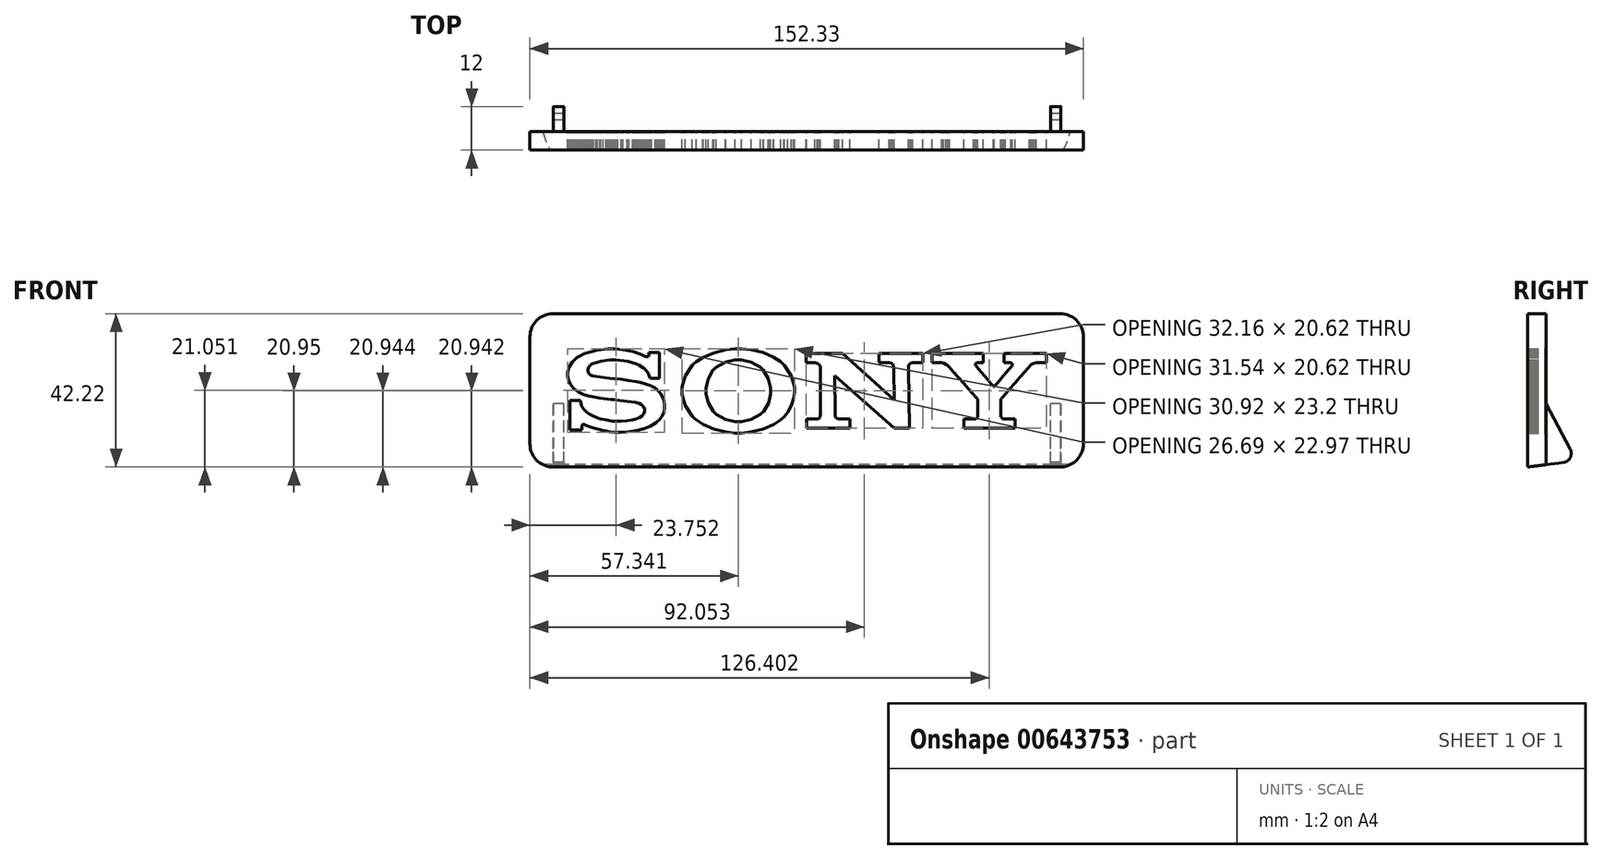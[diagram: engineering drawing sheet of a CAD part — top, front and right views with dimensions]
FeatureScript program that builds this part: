
annotation { "Feature Type Name" : "Feature", "Feature Type Description" : "" }
export const myFeature = defineFeature(function(context is Context, id is Id, definition is map)
    precondition{}
    {
        {
            var Q0;
            Q0=qCreatedBy(makeId("Right.planeOp"),FACE);
            cPlane(context, id + "F0", {"entities" : qUnion([Q0]), "cplaneType" : CPlaneType.OFFSET, "offset" : 69.85 * mm, "width" : 152.4 * mm, "height" : 152.4 * mm});
        }
        {
            var Q0;
            Q0=qCreatedBy(makeId("Right.planeOp"),FACE);
            cPlane(context, id + "F1", {"entities" : qUnion([Q0]), "cplaneType" : CPlaneType.OFFSET, "offset" : 69.85 * mm, "oppositeDirection" : true, "width" : 152.4 * mm, "height" : 152.4 * mm});
        }
        {
            var Q0;
            Q0=qCreatedBy(makeId("Front.planeOp"),FACE);
            var sketch = newSketch(context, id + "F2", { "sketchPlane" : qUnion([Q0])});
            skLineSegment(sketch, "E0.bottom", {"start": v(-69.94, 21.27) * mm, "end": v(69.7, 21.27) * mm});
            skLineSegment(sketch, "E0.top", {"start": v(-69.94, -20.96) * mm, "end": v(69.7, -20.96) * mm});
            skLineSegment(sketch, "E0.left", {"start": v(-76.3, 14.92) * mm, "end": v(-76.3, -14.61) * mm});
            skLineSegment(sketch, "E0.right", {"start": v(76.04, 14.92) * mm, "end": v(76.04, -14.61) * mm});
            skPoint(sketch, "E1.visualSharp", {"position": v(-76.3, 21.27) * mm});
            skArc(sketch, "E1.filletArc", {"start": v(-69.94, 21.27) * mm, "mid": v(-74.43, 19.41) * mm, "end": v(-76.3, 14.92) * mm});
            skPoint(sketch, "E2.visualSharp", {"position": v(-76.3, -20.96) * mm});
            skArc(sketch, "E2.filletArc", {"start": v(-76.3, -14.61) * mm, "mid": v(-74.43, -19.1) * mm, "end": v(-69.94, -20.96) * mm});
            skPoint(sketch, "E3.visualSharp", {"position": v(76.04, 21.27) * mm});
            skArc(sketch, "E3.filletArc", {"start": v(76.04, 14.92) * mm, "mid": v(74.18, 19.41) * mm, "end": v(69.7, 21.27) * mm});
            skPoint(sketch, "E4.visualSharp", {"position": v(76.04, -20.96) * mm});
            skArc(sketch, "E4.filletArc", {"start": v(69.7, -20.96) * mm, "mid": v(74.18, -19.1) * mm, "end": v(76.04, -14.61) * mm});
            skSolve(sketch);
        }
        {
            var Q0;
            Q0 = qSketchRegion(id + "F2", true);
            extrude(context, id + "F3", {"entities" : qUnion([Q0]), "endBound" : BoundingType.SYMMETRIC, "depth" : 5.08 * mm, "offsetDistance" : 25.4 * mm});
        }
        {
            var Q0;
            Q0=qCreatedBy(makeId("Front.planeOp"),FACE);
            var sketch = newSketch(context, id + "F4", { "sketchPlane" : qUnion([Q0])});
            skLineSegment(sketch, "E5", {"start": v(-18.94, -11.6) * mm, "end": v(-19.81, -11.6) * mm});
            skLineSegment(sketch, "E6", {"start": v(-19.81, -11.6) * mm, "end": v(-22.44, -11.33) * mm});
            skLineSegment(sketch, "E7", {"start": v(-22.44, -11.33) * mm, "end": v(-25.7, -10.55) * mm});
            skLineSegment(sketch, "E8", {"start": v(-25.7, -10.55) * mm, "end": v(-28.62, -9.27) * mm});
            skLineSegment(sketch, "E9", {"start": v(-28.62, -9.27) * mm, "end": v(-30.54, -8.02) * mm});
            skLineSegment(sketch, "E10", {"start": v(-30.54, -8.02) * mm, "end": v(-31.1, -7.51) * mm});
            skLineSegment(sketch, "E11", {"start": v(-31.1, -7.51) * mm, "end": v(-31.66, -7.01) * mm});
            skLineSegment(sketch, "E12", {"start": v(-31.66, -7.01) * mm, "end": v(-33.6, -4.05) * mm});
            skLineSegment(sketch, "E13", {"start": v(-33.6, -4.05) * mm, "end": v(-34.4, -1) * mm});
            skLineSegment(sketch, "E14", {"start": v(-34.4, -1) * mm, "end": v(-34.4, 0.02) * mm});
            skLineSegment(sketch, "E15", {"start": v(-34.4, 0.02) * mm, "end": v(-34.4, 1.03) * mm});
            skLineSegment(sketch, "E16", {"start": v(-34.4, 1.03) * mm, "end": v(-33.58, 4.07) * mm});
            skLineSegment(sketch, "E17", {"start": v(-33.58, 4.07) * mm, "end": v(-31.65, 7.03) * mm});
            skLineSegment(sketch, "E18", {"start": v(-31.65, 7.03) * mm, "end": v(-31.1, 7.53) * mm});
            skLineSegment(sketch, "E19", {"start": v(-31.1, 7.53) * mm, "end": v(-30.56, 8.02) * mm});
            skLineSegment(sketch, "E20", {"start": v(-30.56, 8.02) * mm, "end": v(-28.69, 9.22) * mm});
            skLineSegment(sketch, "E21", {"start": v(-28.69, 9.22) * mm, "end": v(-25.7, 10.5) * mm});
            skLineSegment(sketch, "E22", {"start": v(-25.7, 10.5) * mm, "end": v(-22.38, 11.32) * mm});
            skLineSegment(sketch, "E23", {"start": v(-22.38, 11.32) * mm, "end": v(-19.8, 11.6) * mm});
            skLineSegment(sketch, "E24", {"start": v(-19.8, 11.6) * mm, "end": v(-18.94, 11.6) * mm});
            skLineSegment(sketch, "E25", {"start": v(-18.94, 11.6) * mm, "end": v(-18.04, 11.6) * mm});
            skLineSegment(sketch, "E26", {"start": v(-18.04, 11.6) * mm, "end": v(-15.34, 11.36) * mm});
            skLineSegment(sketch, "E27", {"start": v(-15.34, 11.36) * mm, "end": v(-12.11, 10.61) * mm});
            skLineSegment(sketch, "E28", {"start": v(-12.11, 10.61) * mm, "end": v(-9.25, 9.34) * mm});
            skLineSegment(sketch, "E29", {"start": v(-9.25, 9.34) * mm, "end": v(-7.32, 8.04) * mm});
            skLineSegment(sketch, "E30", {"start": v(-7.32, 8.04) * mm, "end": v(-6.75, 7.52) * mm});
            skLineSegment(sketch, "E31", {"start": v(-6.75, 7.52) * mm, "end": v(-6.2, 7.02) * mm});
            skLineSegment(sketch, "E32", {"start": v(-6.2, 7.02) * mm, "end": v(-4.3, 4.06) * mm});
            skLineSegment(sketch, "E33", {"start": v(-4.3, 4.06) * mm, "end": v(-3.49, 1.03) * mm});
            skLineSegment(sketch, "E34", {"start": v(-3.49, 1.03) * mm, "end": v(-3.49, 0.02) * mm});
            skLineSegment(sketch, "E35", {"start": v(-3.49, 0.02) * mm, "end": v(-3.49, -0.49) * mm});
            skLineSegment(sketch, "E36", {"start": v(-3.49, -0.49) * mm, "end": v(-3.7, -2.01) * mm});
            skLineSegment(sketch, "E37", {"start": v(-3.7, -2.01) * mm, "end": v(-4.32, -4.01) * mm});
            skLineSegment(sketch, "E38", {"start": v(-4.32, -4.01) * mm, "end": v(-5.34, -5.88) * mm});
            skLineSegment(sketch, "E39", {"start": v(-5.34, -5.88) * mm, "end": v(-6.36, -7.15) * mm});
            skLineSegment(sketch, "E40", {"start": v(-6.36, -7.15) * mm, "end": v(-6.75, -7.51) * mm});
            skLineSegment(sketch, "E41", {"start": v(-6.75, -7.51) * mm, "end": v(-7.3, -8.02) * mm});
            skLineSegment(sketch, "E42", {"start": v(-7.3, -8.02) * mm, "end": v(-9.2, -9.28) * mm});
            skLineSegment(sketch, "E43", {"start": v(-9.2, -9.28) * mm, "end": v(-12.13, -10.56) * mm});
            skLineSegment(sketch, "E44", {"start": v(-12.13, -10.56) * mm, "end": v(-15.42, -11.34) * mm});
            skLineSegment(sketch, "E45", {"start": v(-15.42, -11.34) * mm, "end": v(-18.06, -11.6) * mm});
            skLineSegment(sketch, "E46", {"start": v(-18.06, -11.6) * mm, "end": v(-18.94, -11.6) * mm});
            skLineSegment(sketch, "E47", {"start": v(-18.94, -11.6) * mm, "end": v(-18.94, -8.54) * mm});
            skLineSegment(sketch, "E48", {"start": v(-18.94, -8.54) * mm, "end": v(-18.04, -8.54) * mm});
            skLineSegment(sketch, "E49", {"start": v(-18.04, -8.54) * mm, "end": v(-15.34, -7.9) * mm});
            skLineSegment(sketch, "E50", {"start": v(-15.34, -7.9) * mm, "end": v(-12.83, -6.44) * mm});
            skLineSegment(sketch, "E51", {"start": v(-12.83, -6.44) * mm, "end": v(-12.41, -6.03) * mm});
            skLineSegment(sketch, "E52", {"start": v(-12.41, -6.03) * mm, "end": v(-12, -5.63) * mm});
            skLineSegment(sketch, "E53", {"start": v(-12, -5.63) * mm, "end": v(-10.61, -3.31) * mm});
            skLineSegment(sketch, "E54", {"start": v(-10.61, -3.31) * mm, "end": v(-10.03, -0.81) * mm});
            skLineSegment(sketch, "E55", {"start": v(-10.03, -0.81) * mm, "end": v(-10.03, 0.02) * mm});
            skLineSegment(sketch, "E56", {"start": v(-10.03, 0.02) * mm, "end": v(-10.03, 0.85) * mm});
            skLineSegment(sketch, "E57", {"start": v(-10.03, 0.85) * mm, "end": v(-10.63, 3.35) * mm});
            skLineSegment(sketch, "E58", {"start": v(-10.63, 3.35) * mm, "end": v(-12.02, 5.7) * mm});
            skLineSegment(sketch, "E59", {"start": v(-12.02, 5.7) * mm, "end": v(-12.41, 6.09) * mm});
            skLineSegment(sketch, "E60", {"start": v(-12.41, 6.09) * mm, "end": v(-12.82, 6.49) * mm});
            skLineSegment(sketch, "E61", {"start": v(-12.82, 6.49) * mm, "end": v(-15.35, 7.93) * mm});
            skLineSegment(sketch, "E62", {"start": v(-15.35, 7.93) * mm, "end": v(-18.04, 8.58) * mm});
            skLineSegment(sketch, "E63", {"start": v(-18.04, 8.58) * mm, "end": v(-18.94, 8.58) * mm});
            skLineSegment(sketch, "E64", {"start": v(-18.94, 8.58) * mm, "end": v(-19.84, 8.58) * mm});
            skLineSegment(sketch, "E65", {"start": v(-19.84, 8.58) * mm, "end": v(-22.54, 7.93) * mm});
            skLineSegment(sketch, "E66", {"start": v(-22.54, 7.93) * mm, "end": v(-25.07, 6.49) * mm});
            skLineSegment(sketch, "E67", {"start": v(-25.07, 6.49) * mm, "end": v(-25.48, 6.09) * mm});
            skLineSegment(sketch, "E68", {"start": v(-25.48, 6.09) * mm, "end": v(-25.87, 5.7) * mm});
            skLineSegment(sketch, "E69", {"start": v(-25.87, 5.7) * mm, "end": v(-27.25, 3.35) * mm});
            skLineSegment(sketch, "E70", {"start": v(-27.25, 3.35) * mm, "end": v(-27.86, 0.85) * mm});
            skLineSegment(sketch, "E71", {"start": v(-27.86, 0.85) * mm, "end": v(-27.86, 0.02) * mm});
            skLineSegment(sketch, "E72", {"start": v(-27.86, 0.02) * mm, "end": v(-27.86, -0.8) * mm});
            skLineSegment(sketch, "E73", {"start": v(-27.86, -0.8) * mm, "end": v(-27.25, -3.3) * mm});
            skLineSegment(sketch, "E74", {"start": v(-27.25, -3.3) * mm, "end": v(-25.86, -5.65) * mm});
            skLineSegment(sketch, "E75", {"start": v(-25.86, -5.65) * mm, "end": v(-25.48, -6.03) * mm});
            skLineSegment(sketch, "E76", {"start": v(-25.48, -6.03) * mm, "end": v(-25.07, -6.43) * mm});
            skLineSegment(sketch, "E77", {"start": v(-25.07, -6.43) * mm, "end": v(-22.54, -7.9) * mm});
            skLineSegment(sketch, "E78", {"start": v(-22.54, -7.9) * mm, "end": v(-19.84, -8.54) * mm});
            skLineSegment(sketch, "E79", {"start": v(-19.84, -8.54) * mm, "end": v(-18.94, -8.54) * mm});
            skLineSegment(sketch, "E80", {"start": v(-18.94, -8.54) * mm, "end": v(-18.94, -11.6) * mm});
            skLineSegment(sketch, "E81", {"start": v(-53.83, 11.59) * mm, "end": v(-54.83, 11.59) * mm});
            skLineSegment(sketch, "E82", {"start": v(-54.83, 11.59) * mm, "end": v(-57.82, 11.21) * mm});
            skLineSegment(sketch, "E83", {"start": v(-57.82, 11.21) * mm, "end": v(-61.13, 10.29) * mm});
            skLineSegment(sketch, "E84", {"start": v(-61.13, 10.29) * mm, "end": v(-61.74, 10.01) * mm});
            skLineSegment(sketch, "E85", {"start": v(-61.74, 10.01) * mm, "end": v(-62.16, 9.82) * mm});
            skLineSegment(sketch, "E86", {"start": v(-62.16, 9.82) * mm, "end": v(-63.35, 9.12) * mm});
            skLineSegment(sketch, "E87", {"start": v(-63.35, 9.12) * mm, "end": v(-64.67, 7.96) * mm});
            skLineSegment(sketch, "E88", {"start": v(-64.67, 7.96) * mm, "end": v(-65.56, 6.48) * mm});
            skLineSegment(sketch, "E89", {"start": v(-65.56, 6.48) * mm, "end": v(-65.88, 5.1) * mm});
            skLineSegment(sketch, "E90", {"start": v(-65.88, 5.1) * mm, "end": v(-65.88, 4.63) * mm});
            skLineSegment(sketch, "E91", {"start": v(-65.88, 4.63) * mm, "end": v(-65.88, 4.22) * mm});
            skLineSegment(sketch, "E92", {"start": v(-65.88, 4.22) * mm, "end": v(-65.64, 3) * mm});
            skLineSegment(sketch, "E93", {"start": v(-65.64, 3) * mm, "end": v(-65.1, 1.77) * mm});
            skLineSegment(sketch, "E94", {"start": v(-65.1, 1.77) * mm, "end": v(-64.59, 1.03) * mm});
            skLineSegment(sketch, "E95", {"start": v(-64.59, 1.03) * mm, "end": v(-64.37, 0.79) * mm});
            skLineSegment(sketch, "E96", {"start": v(-64.37, 0.79) * mm, "end": v(-64.22, 0.65) * mm});
            skLineSegment(sketch, "E97", {"start": v(-64.22, 0.65) * mm, "end": v(-63.77, 0.26) * mm});
            skLineSegment(sketch, "E98", {"start": v(-63.77, 0.26) * mm, "end": v(-62.9, -0.34) * mm});
            skLineSegment(sketch, "E99", {"start": v(-62.9, -0.34) * mm, "end": v(-61.64, -0.95) * mm});
            skLineSegment(sketch, "E100", {"start": v(-61.64, -0.95) * mm, "end": v(-60.3, -1.37) * mm});
            skLineSegment(sketch, "E101", {"start": v(-60.3, -1.37) * mm, "end": v(-59.85, -1.47) * mm});
            skLineSegment(sketch, "E102", {"start": v(-59.85, -1.47) * mm, "end": v(-59.54, -1.54) * mm});
            skLineSegment(sketch, "E103", {"start": v(-59.54, -1.54) * mm, "end": v(-57.1, -1.95) * mm});
            skLineSegment(sketch, "E104", {"start": v(-57.1, -1.95) * mm, "end": v(-53.95, -2.37) * mm});
            skLineSegment(sketch, "E105", {"start": v(-53.95, -2.37) * mm, "end": v(-53.29, -2.44) * mm});
            skLineSegment(sketch, "E106", {"start": v(-53.29, -2.44) * mm, "end": v(-52.63, -2.5) * mm});
            skLineSegment(sketch, "E107", {"start": v(-52.63, -2.5) * mm, "end": v(-49.55, -2.85) * mm});
            skLineSegment(sketch, "E108", {"start": v(-49.55, -2.85) * mm, "end": v(-47.27, -3.18) * mm});
            skLineSegment(sketch, "E109", {"start": v(-47.27, -3.18) * mm, "end": v(-47, -3.25) * mm});
            skLineSegment(sketch, "E110", {"start": v(-47, -3.25) * mm, "end": v(-46.83, -3.3) * mm});
            skLineSegment(sketch, "E111", {"start": v(-46.83, -3.3) * mm, "end": v(-46.3, -3.44) * mm});
            skLineSegment(sketch, "E112", {"start": v(-46.3, -3.44) * mm, "end": v(-45.57, -3.78) * mm});
            skLineSegment(sketch, "E113", {"start": v(-45.57, -3.78) * mm, "end": v(-45, -4.37) * mm});
            skLineSegment(sketch, "E114", {"start": v(-45, -4.37) * mm, "end": v(-44.76, -5.1) * mm});
            skLineSegment(sketch, "E115", {"start": v(-44.76, -5.1) * mm, "end": v(-44.76, -5.34) * mm});
            skLineSegment(sketch, "E116", {"start": v(-44.76, -5.34) * mm, "end": v(-44.76, -5.58) * mm});
            skLineSegment(sketch, "E117", {"start": v(-44.76, -5.58) * mm, "end": v(-45, -6.32) * mm});
            skLineSegment(sketch, "E118", {"start": v(-45, -6.32) * mm, "end": v(-45.53, -6.97) * mm});
            skLineSegment(sketch, "E119", {"start": v(-45.53, -6.97) * mm, "end": v(-46.12, -7.33) * mm});
            skLineSegment(sketch, "E120", {"start": v(-46.12, -7.33) * mm, "end": v(-46.44, -7.47) * mm});
            skLineSegment(sketch, "E121", {"start": v(-46.44, -7.47) * mm, "end": v(-46.5, -7.5) * mm});
            skLineSegment(sketch, "E122", {"start": v(-46.5, -7.5) * mm, "end": v(-46.56, -7.52) * mm});
            skLineSegment(sketch, "E123", {"start": v(-46.56, -7.52) * mm, "end": v(-46.98, -7.68) * mm});
            skLineSegment(sketch, "E124", {"start": v(-46.98, -7.68) * mm, "end": v(-48.02, -8) * mm});
            skLineSegment(sketch, "E125", {"start": v(-48.02, -8) * mm, "end": v(-49.6, -8.28) * mm});
            skLineSegment(sketch, "E126", {"start": v(-49.6, -8.28) * mm, "end": v(-51.2, -8.41) * mm});
            skLineSegment(sketch, "E127", {"start": v(-51.2, -8.41) * mm, "end": v(-51.74, -8.41) * mm});
            skLineSegment(sketch, "E128", {"start": v(-51.74, -8.41) * mm, "end": v(-52.2, -8.41) * mm});
            skLineSegment(sketch, "E129", {"start": v(-52.2, -8.41) * mm, "end": v(-53.57, -8.3) * mm});
            skLineSegment(sketch, "E130", {"start": v(-53.57, -8.3) * mm, "end": v(-55.36, -8.01) * mm});
            skLineSegment(sketch, "E131", {"start": v(-55.36, -8.01) * mm, "end": v(-56.9, -7.66) * mm});
            skLineSegment(sketch, "E132", {"start": v(-56.9, -7.66) * mm, "end": v(-57.72, -7.42) * mm});
            skLineSegment(sketch, "E133", {"start": v(-57.72, -7.42) * mm, "end": v(-57.98, -7.33) * mm});
            skLineSegment(sketch, "E134", {"start": v(-57.98, -7.33) * mm, "end": v(-58.2, -7.25) * mm});
            skLineSegment(sketch, "E135", {"start": v(-58.2, -7.25) * mm, "end": v(-58.88, -6.98) * mm});
            skLineSegment(sketch, "E136", {"start": v(-58.88, -6.98) * mm, "end": v(-59.8, -6.5) * mm});
            skLineSegment(sketch, "E137", {"start": v(-59.8, -6.5) * mm, "end": v(-60.7, -5.84) * mm});
            skLineSegment(sketch, "E138", {"start": v(-60.7, -5.84) * mm, "end": v(-61.4, -5.16) * mm});
            skLineSegment(sketch, "E139", {"start": v(-61.4, -5.16) * mm, "end": v(-61.6, -4.92) * mm});
            skLineSegment(sketch, "E140", {"start": v(-61.6, -4.92) * mm, "end": v(-61.66, -4.83) * mm});
            skLineSegment(sketch, "E141", {"start": v(-61.66, -4.83) * mm, "end": v(-61.83, -4.55) * mm});
            skLineSegment(sketch, "E142", {"start": v(-61.83, -4.55) * mm, "end": v(-62.08, -4) * mm});
            skLineSegment(sketch, "E143", {"start": v(-62.08, -4) * mm, "end": v(-62.27, -3.34) * mm});
            skLineSegment(sketch, "E144", {"start": v(-62.27, -3.34) * mm, "end": v(-62.34, -2.8) * mm});
            skLineSegment(sketch, "E145", {"start": v(-62.34, -2.8) * mm, "end": v(-62.34, -2.63) * mm});
            skLineSegment(sketch, "E146", {"start": v(-62.34, -2.63) * mm, "end": v(-65.24, -2.63) * mm});
            skLineSegment(sketch, "E147", {"start": v(-65.24, -2.63) * mm, "end": v(-65.24, -10.75) * mm});
            skLineSegment(sketch, "E148", {"start": v(-65.24, -10.75) * mm, "end": v(-62.02, -10.75) * mm});
            skLineSegment(sketch, "E149", {"start": v(-62.02, -10.75) * mm, "end": v(-62.02, -9.65) * mm});
            skLineSegment(sketch, "E150", {"start": v(-62.02, -9.65) * mm, "end": v(-62.02, -9.61) * mm});
            skLineSegment(sketch, "E151", {"start": v(-62.02, -9.61) * mm, "end": v(-61.99, -9.5) * mm});
            skLineSegment(sketch, "E152", {"start": v(-61.99, -9.5) * mm, "end": v(-61.87, -9.31) * mm});
            skLineSegment(sketch, "E153", {"start": v(-61.87, -9.31) * mm, "end": v(-61.66, -9.2) * mm});
            skLineSegment(sketch, "E154", {"start": v(-61.66, -9.2) * mm, "end": v(-61.4, -9.22) * mm});
            skLineSegment(sketch, "E155", {"start": v(-61.4, -9.22) * mm, "end": v(-61.32, -9.25) * mm});
            skLineSegment(sketch, "E156", {"start": v(-61.32, -9.25) * mm, "end": v(-61.15, -9.33) * mm});
            skLineSegment(sketch, "E157", {"start": v(-61.15, -9.33) * mm, "end": v(-60.6, -9.56) * mm});
            skLineSegment(sketch, "E158", {"start": v(-60.6, -9.56) * mm, "end": v(-59.49, -9.97) * mm});
            skLineSegment(sketch, "E159", {"start": v(-59.49, -9.97) * mm, "end": v(-58.12, -10.4) * mm});
            skLineSegment(sketch, "E160", {"start": v(-58.12, -10.4) * mm, "end": v(-57, -10.7) * mm});
            skLineSegment(sketch, "E161", {"start": v(-57, -10.7) * mm, "end": v(-56.6, -10.78) * mm});
            skLineSegment(sketch, "E162", {"start": v(-56.6, -10.78) * mm, "end": v(-56.31, -10.84) * mm});
            skLineSegment(sketch, "E163", {"start": v(-56.31, -10.84) * mm, "end": v(-55.43, -11.02) * mm});
            skLineSegment(sketch, "E164", {"start": v(-55.43, -11.02) * mm, "end": v(-54.32, -11.21) * mm});
            skLineSegment(sketch, "E165", {"start": v(-54.32, -11.21) * mm, "end": v(-53.14, -11.34) * mm});
            skLineSegment(sketch, "E166", {"start": v(-53.14, -11.34) * mm, "end": v(-52.08, -11.39) * mm});
            skLineSegment(sketch, "E167", {"start": v(-52.08, -11.39) * mm, "end": v(-51.72, -11.39) * mm});
            skLineSegment(sketch, "E168", {"start": v(-51.72, -11.39) * mm, "end": v(-51.15, -11.39) * mm});
            skLineSegment(sketch, "E169", {"start": v(-51.15, -11.39) * mm, "end": v(-49.43, -11.3) * mm});
            skLineSegment(sketch, "E170", {"start": v(-49.43, -11.3) * mm, "end": v(-47.64, -11.06) * mm});
            skLineSegment(sketch, "E171", {"start": v(-47.64, -11.06) * mm, "end": v(-46.25, -10.76) * mm});
            skLineSegment(sketch, "E172", {"start": v(-46.25, -10.76) * mm, "end": v(-45.44, -10.54) * mm});
            skLineSegment(sketch, "E173", {"start": v(-45.44, -10.54) * mm, "end": v(-45.17, -10.46) * mm});
            skLineSegment(sketch, "E174", {"start": v(-45.17, -10.46) * mm, "end": v(-44.87, -10.38) * mm});
            skLineSegment(sketch, "E175", {"start": v(-44.87, -10.38) * mm, "end": v(-43.23, -9.73) * mm});
            skLineSegment(sketch, "E176", {"start": v(-43.23, -9.73) * mm, "end": v(-41.58, -8.78) * mm});
            skLineSegment(sketch, "E177", {"start": v(-41.58, -8.78) * mm, "end": v(-41.28, -8.54) * mm});
            skLineSegment(sketch, "E178", {"start": v(-41.28, -8.54) * mm, "end": v(-41.12, -8.41) * mm});
            skLineSegment(sketch, "E179", {"start": v(-41.12, -8.41) * mm, "end": v(-40.68, -8) * mm});
            skLineSegment(sketch, "E180", {"start": v(-40.68, -8) * mm, "end": v(-40, -7.11) * mm});
            skLineSegment(sketch, "E181", {"start": v(-40, -7.11) * mm, "end": v(-39.43, -5.88) * mm});
            skLineSegment(sketch, "E182", {"start": v(-39.43, -5.88) * mm, "end": v(-39.2, -4.67) * mm});
            skLineSegment(sketch, "E183", {"start": v(-39.2, -4.67) * mm, "end": v(-39.2, -4.27) * mm});
            skLineSegment(sketch, "E184", {"start": v(-39.2, -4.27) * mm, "end": v(-39.2, -3.87) * mm});
            skLineSegment(sketch, "E185", {"start": v(-39.2, -3.87) * mm, "end": v(-39.4, -2.7) * mm});
            skLineSegment(sketch, "E186", {"start": v(-39.4, -2.7) * mm, "end": v(-39.87, -1.46) * mm});
            skLineSegment(sketch, "E187", {"start": v(-39.87, -1.46) * mm, "end": v(-40.43, -0.58) * mm});
            skLineSegment(sketch, "E188", {"start": v(-40.43, -0.58) * mm, "end": v(-40.77, -0.18) * mm});
            skLineSegment(sketch, "E189", {"start": v(-40.77, -0.18) * mm, "end": v(-40.88, -0.07) * mm});
            skLineSegment(sketch, "E190", {"start": v(-40.88, -0.07) * mm, "end": v(-41.03, 0.08) * mm});
            skLineSegment(sketch, "E191", {"start": v(-41.03, 0.08) * mm, "end": v(-41.86, 0.73) * mm});
            skLineSegment(sketch, "E192", {"start": v(-41.86, 0.73) * mm, "end": v(-42.78, 1.26) * mm});
            skLineSegment(sketch, "E193", {"start": v(-42.78, 1.26) * mm, "end": v(-42.96, 1.35) * mm});
            skLineSegment(sketch, "E194", {"start": v(-42.96, 1.35) * mm, "end": v(-43.13, 1.43) * mm});
            skLineSegment(sketch, "E195", {"start": v(-43.13, 1.43) * mm, "end": v(-44.17, 1.84) * mm});
            skLineSegment(sketch, "E196", {"start": v(-44.17, 1.84) * mm, "end": v(-45.31, 2.2) * mm});
            skLineSegment(sketch, "E197", {"start": v(-45.31, 2.2) * mm, "end": v(-45.53, 2.25) * mm});
            skLineSegment(sketch, "E198", {"start": v(-45.53, 2.25) * mm, "end": v(-45.92, 2.34) * mm});
            skLineSegment(sketch, "E199", {"start": v(-45.92, 2.34) * mm, "end": v(-47.1, 2.56) * mm});
            skLineSegment(sketch, "E200", {"start": v(-47.1, 2.56) * mm, "end": v(-49.08, 2.88) * mm});
            skLineSegment(sketch, "E201", {"start": v(-49.08, 2.88) * mm, "end": v(-51.09, 3.15) * mm});
            skLineSegment(sketch, "E202", {"start": v(-51.09, 3.15) * mm, "end": v(-52.32, 3.3) * mm});
            skLineSegment(sketch, "E203", {"start": v(-52.32, 3.3) * mm, "end": v(-52.73, 3.35) * mm});
            skLineSegment(sketch, "E204", {"start": v(-52.73, 3.35) * mm, "end": v(-53.14, 3.39) * mm});
            skLineSegment(sketch, "E205", {"start": v(-53.14, 3.39) * mm, "end": v(-54.35, 3.5) * mm});
            skLineSegment(sketch, "E206", {"start": v(-54.35, 3.5) * mm, "end": v(-56.18, 3.7) * mm});
            skLineSegment(sketch, "E207", {"start": v(-56.18, 3.7) * mm, "end": v(-57.9, 3.94) * mm});
            skLineSegment(sketch, "E208", {"start": v(-57.9, 3.94) * mm, "end": v(-58.87, 4.12) * mm});
            skLineSegment(sketch, "E209", {"start": v(-58.87, 4.12) * mm, "end": v(-59.19, 4.22) * mm});
            skLineSegment(sketch, "E210", {"start": v(-59.19, 4.22) * mm, "end": v(-59.28, 4.24) * mm});
            skLineSegment(sketch, "E211", {"start": v(-59.28, 4.24) * mm, "end": v(-59.54, 4.36) * mm});
            skLineSegment(sketch, "E212", {"start": v(-59.54, 4.36) * mm, "end": v(-59.94, 4.63) * mm});
            skLineSegment(sketch, "E213", {"start": v(-59.94, 4.63) * mm, "end": v(-60.25, 5.06) * mm});
            skLineSegment(sketch, "E214", {"start": v(-60.25, 5.06) * mm, "end": v(-60.39, 5.5) * mm});
            skLineSegment(sketch, "E215", {"start": v(-60.39, 5.5) * mm, "end": v(-60.39, 5.66) * mm});
            skLineSegment(sketch, "E216", {"start": v(-60.39, 5.66) * mm, "end": v(-60.39, 5.89) * mm});
            skLineSegment(sketch, "E217", {"start": v(-60.39, 5.89) * mm, "end": v(-60.11, 6.58) * mm});
            skLineSegment(sketch, "E218", {"start": v(-60.11, 6.58) * mm, "end": v(-59.47, 7.23) * mm});
            skLineSegment(sketch, "E219", {"start": v(-59.47, 7.23) * mm, "end": v(-59.29, 7.34) * mm});
            skLineSegment(sketch, "E220", {"start": v(-59.29, 7.34) * mm, "end": v(-59, 7.53) * mm});
            skLineSegment(sketch, "E221", {"start": v(-59, 7.53) * mm, "end": v(-56.8, 8.2) * mm});
            skLineSegment(sketch, "E222", {"start": v(-56.8, 8.2) * mm, "end": v(-54.22, 8.52) * mm});
            skLineSegment(sketch, "E223", {"start": v(-54.22, 8.52) * mm, "end": v(-53.36, 8.52) * mm});
            skLineSegment(sketch, "E224", {"start": v(-53.36, 8.52) * mm, "end": v(-52.64, 8.52) * mm});
            skLineSegment(sketch, "E225", {"start": v(-52.64, 8.52) * mm, "end": v(-49.43, 8.11) * mm});
            skLineSegment(sketch, "E226", {"start": v(-49.43, 8.11) * mm, "end": v(-46.89, 7.35) * mm});
            skLineSegment(sketch, "E227", {"start": v(-46.89, 7.35) * mm, "end": v(-46.5, 7.18) * mm});
            skLineSegment(sketch, "E228", {"start": v(-46.5, 7.18) * mm, "end": v(-46.37, 7.12) * mm});
            skLineSegment(sketch, "E229", {"start": v(-46.37, 7.12) * mm, "end": v(-44.99, 6.3) * mm});
            skLineSegment(sketch, "E230", {"start": v(-44.99, 6.3) * mm, "end": v(-44.86, 6.2) * mm});
            skLineSegment(sketch, "E231", {"start": v(-44.86, 6.2) * mm, "end": v(-44.74, 6.1) * mm});
            skLineSegment(sketch, "E232", {"start": v(-44.74, 6.1) * mm, "end": v(-44.42, 5.78) * mm});
            skLineSegment(sketch, "E233", {"start": v(-44.42, 5.78) * mm, "end": v(-43.96, 5.18) * mm});
            skLineSegment(sketch, "E234", {"start": v(-43.96, 5.18) * mm, "end": v(-43.55, 4.42) * mm});
            skLineSegment(sketch, "E235", {"start": v(-43.55, 4.42) * mm, "end": v(-43.3, 3.74) * mm});
            skLineSegment(sketch, "E236", {"start": v(-43.3, 3.74) * mm, "end": v(-43.25, 3.5) * mm});
            skLineSegment(sketch, "E237", {"start": v(-43.25, 3.5) * mm, "end": v(-40.65, 3.5) * mm});
            skLineSegment(sketch, "E238", {"start": v(-40.65, 3.5) * mm, "end": v(-40.65, 10.58) * mm});
            skLineSegment(sketch, "E239", {"start": v(-40.65, 10.58) * mm, "end": v(-43.56, 10.58) * mm});
            skLineSegment(sketch, "E240", {"start": v(-43.56, 10.58) * mm, "end": v(-43.56, 9.75) * mm});
            skLineSegment(sketch, "E241", {"start": v(-43.56, 9.75) * mm, "end": v(-43.56, 9.66) * mm});
            skLineSegment(sketch, "E242", {"start": v(-43.56, 9.66) * mm, "end": v(-43.76, 9.39) * mm});
            skLineSegment(sketch, "E243", {"start": v(-43.76, 9.39) * mm, "end": v(-44.23, 9.37) * mm});
            skLineSegment(sketch, "E244", {"start": v(-44.23, 9.37) * mm, "end": v(-44.35, 9.43) * mm});
            skLineSegment(sketch, "E245", {"start": v(-44.35, 9.43) * mm, "end": v(-44.67, 9.6) * mm});
            skLineSegment(sketch, "E246", {"start": v(-44.67, 9.6) * mm, "end": v(-45.74, 10.05) * mm});
            skLineSegment(sketch, "E247", {"start": v(-45.74, 10.05) * mm, "end": v(-47.89, 10.76) * mm});
            skLineSegment(sketch, "E248", {"start": v(-47.89, 10.76) * mm, "end": v(-50.63, 11.35) * mm});
            skLineSegment(sketch, "E249", {"start": v(-50.63, 11.35) * mm, "end": v(-53.03, 11.59) * mm});
            skLineSegment(sketch, "E250", {"start": v(-53.03, 11.59) * mm, "end": v(-53.83, 11.59) * mm});
            skLineSegment(sketch, "E251", {"start": v(9.81, 10.3) * mm, "end": v(23.98, -2.48) * mm});
            skLineSegment(sketch, "E252", {"start": v(23.98, -2.48) * mm, "end": v(23.84, 6.13) * mm});
            skLineSegment(sketch, "E253", {"start": v(23.84, 6.13) * mm, "end": v(23.83, 6.3) * mm});
            skLineSegment(sketch, "E254", {"start": v(23.83, 6.3) * mm, "end": v(23.78, 6.85) * mm});
            skLineSegment(sketch, "E255", {"start": v(23.78, 6.85) * mm, "end": v(23.57, 7.35) * mm});
            skLineSegment(sketch, "E256", {"start": v(23.57, 7.35) * mm, "end": v(23.13, 7.64) * mm});
            skLineSegment(sketch, "E257", {"start": v(23.13, 7.64) * mm, "end": v(22.58, 7.73) * mm});
            skLineSegment(sketch, "E258", {"start": v(22.58, 7.73) * mm, "end": v(22.4, 7.73) * mm});
            skLineSegment(sketch, "E259", {"start": v(22.4, 7.73) * mm, "end": v(19.73, 7.73) * mm});
            skLineSegment(sketch, "E260", {"start": v(19.73, 7.73) * mm, "end": v(19.73, 10.3) * mm});
            skLineSegment(sketch, "E261", {"start": v(19.73, 10.3) * mm, "end": v(31.84, 10.3) * mm});
            skLineSegment(sketch, "E262", {"start": v(31.84, 10.3) * mm, "end": v(31.84, 7.73) * mm});
            skLineSegment(sketch, "E263", {"start": v(31.84, 7.73) * mm, "end": v(29.24, 7.73) * mm});
            skLineSegment(sketch, "E264", {"start": v(29.24, 7.73) * mm, "end": v(29.06, 7.73) * mm});
            skLineSegment(sketch, "E265", {"start": v(29.06, 7.73) * mm, "end": v(28.51, 7.65) * mm});
            skLineSegment(sketch, "E266", {"start": v(28.51, 7.65) * mm, "end": v(28.11, 7.38) * mm});
            skLineSegment(sketch, "E267", {"start": v(28.11, 7.38) * mm, "end": v(27.95, 6.88) * mm});
            skLineSegment(sketch, "E268", {"start": v(27.95, 6.88) * mm, "end": v(27.9, 6.32) * mm});
            skLineSegment(sketch, "E269", {"start": v(27.9, 6.32) * mm, "end": v(27.9, 6.13) * mm});
            skLineSegment(sketch, "E270", {"start": v(27.9, 6.13) * mm, "end": v(28.12, -10.32) * mm});
            skLineSegment(sketch, "E271", {"start": v(28.12, -10.32) * mm, "end": v(23.98, -10.32) * mm});
            skLineSegment(sketch, "E272", {"start": v(23.98, -10.32) * mm, "end": v(7.66, 4.24) * mm});
            skLineSegment(sketch, "E273", {"start": v(7.66, 4.24) * mm, "end": v(7.66, -6.1) * mm});
            skLineSegment(sketch, "E274", {"start": v(7.66, -6.1) * mm, "end": v(7.66, -6.27) * mm});
            skLineSegment(sketch, "E275", {"start": v(7.66, -6.27) * mm, "end": v(7.7, -6.82) * mm});
            skLineSegment(sketch, "E276", {"start": v(7.7, -6.82) * mm, "end": v(7.85, -7.34) * mm});
            skLineSegment(sketch, "E277", {"start": v(7.85, -7.34) * mm, "end": v(8.2, -7.65) * mm});
            skLineSegment(sketch, "E278", {"start": v(8.2, -7.65) * mm, "end": v(8.72, -7.75) * mm});
            skLineSegment(sketch, "E279", {"start": v(8.72, -7.75) * mm, "end": v(8.89, -7.75) * mm});
            skLineSegment(sketch, "E280", {"start": v(8.89, -7.75) * mm, "end": v(11.8, -7.75) * mm});
            skLineSegment(sketch, "E281", {"start": v(11.8, -7.75) * mm, "end": v(11.8, -10.32) * mm});
            skLineSegment(sketch, "E282", {"start": v(11.8, -10.32) * mm, "end": v(-0.1, -10.32) * mm});
            skLineSegment(sketch, "E283", {"start": v(-0.1, -10.32) * mm, "end": v(-0.1, -7.75) * mm});
            skLineSegment(sketch, "E284", {"start": v(-0.1, -7.75) * mm, "end": v(2.68, -7.75) * mm});
            skLineSegment(sketch, "E285", {"start": v(2.68, -7.75) * mm, "end": v(2.83, -7.75) * mm});
            skLineSegment(sketch, "E286", {"start": v(2.83, -7.75) * mm, "end": v(3.28, -7.58) * mm});
            skLineSegment(sketch, "E287", {"start": v(3.28, -7.58) * mm, "end": v(3.57, -7.16) * mm});
            skLineSegment(sketch, "E288", {"start": v(3.57, -7.16) * mm, "end": v(3.67, -6.6) * mm});
            skLineSegment(sketch, "E289", {"start": v(3.67, -6.6) * mm, "end": v(3.68, -6.18) * mm});
            skLineSegment(sketch, "E290", {"start": v(3.68, -6.18) * mm, "end": v(3.68, -6.03) * mm});
            skLineSegment(sketch, "E291", {"start": v(3.68, -6.03) * mm, "end": v(3.68, 6.03) * mm});
            skLineSegment(sketch, "E292", {"start": v(3.68, 6.03) * mm, "end": v(3.68, 6.18) * mm});
            skLineSegment(sketch, "E293", {"start": v(3.68, 6.18) * mm, "end": v(3.64, 6.62) * mm});
            skLineSegment(sketch, "E294", {"start": v(3.64, 6.62) * mm, "end": v(3.42, 7.17) * mm});
            skLineSegment(sketch, "E295", {"start": v(3.42, 7.17) * mm, "end": v(2.9, 7.57) * mm});
            skLineSegment(sketch, "E296", {"start": v(2.9, 7.57) * mm, "end": v(2.18, 7.73) * mm});
            skLineSegment(sketch, "E297", {"start": v(2.18, 7.73) * mm, "end": v(1.94, 7.73) * mm});
            skLineSegment(sketch, "E298", {"start": v(1.94, 7.73) * mm, "end": v(-0.32, 7.73) * mm});
            skLineSegment(sketch, "E299", {"start": v(-0.32, 7.73) * mm, "end": v(-0.32, 10.3) * mm});
            skLineSegment(sketch, "E300", {"start": v(-0.32, 10.3) * mm, "end": v(9.81, 10.3) * mm});
            skLineSegment(sketch, "E301", {"start": v(45.68, -7.74) * mm, "end": v(45.77, -7.74) * mm});
            skLineSegment(sketch, "E302", {"start": v(45.77, -7.74) * mm, "end": v(46.05, -7.73) * mm});
            skLineSegment(sketch, "E303", {"start": v(46.05, -7.73) * mm, "end": v(46.38, -7.7) * mm});
            skLineSegment(sketch, "E304", {"start": v(46.38, -7.7) * mm, "end": v(46.4, -7.7) * mm});
            skLineSegment(sketch, "E305", {"start": v(46.4, -7.7) * mm, "end": v(46.47, -7.67) * mm});
            skLineSegment(sketch, "E306", {"start": v(46.47, -7.67) * mm, "end": v(46.93, -7.25) * mm});
            skLineSegment(sketch, "E307", {"start": v(46.93, -7.25) * mm, "end": v(46.96, -7.2) * mm});
            skLineSegment(sketch, "E308", {"start": v(46.96, -7.2) * mm, "end": v(46.96, -7.18) * mm});
            skLineSegment(sketch, "E309", {"start": v(46.96, -7.18) * mm, "end": v(47, -6.92) * mm});
            skLineSegment(sketch, "E310", {"start": v(47, -6.92) * mm, "end": v(47.01, -6.71) * mm});
            skLineSegment(sketch, "E311", {"start": v(47.01, -6.71) * mm, "end": v(47.01, -6.64) * mm});
            skLineSegment(sketch, "E312", {"start": v(47.01, -6.64) * mm, "end": v(47.01, -2.57) * mm});
            skLineSegment(sketch, "E313", {"start": v(47.01, -2.57) * mm, "end": v(47.01, -2.54) * mm});
            skLineSegment(sketch, "E314", {"start": v(47.01, -2.54) * mm, "end": v(46.99, -2.44) * mm});
            skLineSegment(sketch, "E315", {"start": v(46.99, -2.44) * mm, "end": v(46.88, -2.27) * mm});
            skLineSegment(sketch, "E316", {"start": v(46.88, -2.27) * mm, "end": v(46.84, -2.22) * mm});
            skLineSegment(sketch, "E317", {"start": v(46.84, -2.22) * mm, "end": v(46.8, -2.16) * mm});
            skLineSegment(sketch, "E318", {"start": v(46.8, -2.16) * mm, "end": v(46.47, -1.78) * mm});
            skLineSegment(sketch, "E319", {"start": v(46.47, -1.78) * mm, "end": v(45.6, -0.8) * mm});
            skLineSegment(sketch, "E320", {"start": v(45.6, -0.8) * mm, "end": v(44.4, 0.58) * mm});
            skLineSegment(sketch, "E321", {"start": v(44.4, 0.58) * mm, "end": v(43.02, 2.14) * mm});
            skLineSegment(sketch, "E322", {"start": v(43.02, 2.14) * mm, "end": v(41.64, 3.7) * mm});
            skLineSegment(sketch, "E323", {"start": v(41.64, 3.7) * mm, "end": v(40.42, 5.1) * mm});
            skLineSegment(sketch, "E324", {"start": v(40.42, 5.1) * mm, "end": v(39.5, 6.11) * mm});
            skLineSegment(sketch, "E325", {"start": v(39.5, 6.11) * mm, "end": v(39.17, 6.5) * mm});
            skLineSegment(sketch, "E326", {"start": v(39.17, 6.5) * mm, "end": v(39.09, 6.58) * mm});
            skLineSegment(sketch, "E327", {"start": v(39.09, 6.58) * mm, "end": v(39, 6.68) * mm});
            skLineSegment(sketch, "E328", {"start": v(39, 6.68) * mm, "end": v(38.72, 6.95) * mm});
            skLineSegment(sketch, "E329", {"start": v(38.72, 6.95) * mm, "end": v(38.23, 7.32) * mm});
            skLineSegment(sketch, "E330", {"start": v(38.23, 7.32) * mm, "end": v(37.61, 7.61) * mm});
            skLineSegment(sketch, "E331", {"start": v(37.61, 7.61) * mm, "end": v(37.05, 7.73) * mm});
            skLineSegment(sketch, "E332", {"start": v(37.05, 7.73) * mm, "end": v(36.86, 7.73) * mm});
            skLineSegment(sketch, "E333", {"start": v(36.86, 7.73) * mm, "end": v(34.34, 7.73) * mm});
            skLineSegment(sketch, "E334", {"start": v(34.34, 7.73) * mm, "end": v(34.34, 10.3) * mm});
            skLineSegment(sketch, "E335", {"start": v(34.34, 10.3) * mm, "end": v(48.55, 10.3) * mm});
            skLineSegment(sketch, "E336", {"start": v(48.55, 10.3) * mm, "end": v(48.55, 7.73) * mm});
            skLineSegment(sketch, "E337", {"start": v(48.55, 7.73) * mm, "end": v(46.83, 7.73) * mm});
            skLineSegment(sketch, "E338", {"start": v(46.83, 7.73) * mm, "end": v(46.77, 7.73) * mm});
            skLineSegment(sketch, "E339", {"start": v(46.77, 7.73) * mm, "end": v(46.57, 7.66) * mm});
            skLineSegment(sketch, "E340", {"start": v(46.57, 7.66) * mm, "end": v(46.4, 7.5) * mm});
            skLineSegment(sketch, "E341", {"start": v(46.4, 7.5) * mm, "end": v(46.36, 7.24) * mm});
            skLineSegment(sketch, "E342", {"start": v(46.36, 7.24) * mm, "end": v(46.46, 7) * mm});
            skLineSegment(sketch, "E343", {"start": v(46.46, 7) * mm, "end": v(46.51, 6.94) * mm});
            skLineSegment(sketch, "E344", {"start": v(46.51, 6.94) * mm, "end": v(46.72, 6.7) * mm});
            skLineSegment(sketch, "E345", {"start": v(46.72, 6.7) * mm, "end": v(47.26, 6.04) * mm});
            skLineSegment(sketch, "E346", {"start": v(47.26, 6.04) * mm, "end": v(48.03, 5.12) * mm});
            skLineSegment(sketch, "E347", {"start": v(48.03, 5.12) * mm, "end": v(48.9, 4.07) * mm});
            skLineSegment(sketch, "E348", {"start": v(48.9, 4.07) * mm, "end": v(49.79, 3.02) * mm});
            skLineSegment(sketch, "E349", {"start": v(49.79, 3.02) * mm, "end": v(50.56, 2.09) * mm});
            skLineSegment(sketch, "E350", {"start": v(50.56, 2.09) * mm, "end": v(51.12, 1.43) * mm});
            skLineSegment(sketch, "E351", {"start": v(51.12, 1.43) * mm, "end": v(51.32, 1.18) * mm});
            skLineSegment(sketch, "E352", {"start": v(51.32, 1.18) * mm, "end": v(51.34, 1.16) * mm});
            skLineSegment(sketch, "E353", {"start": v(51.34, 1.16) * mm, "end": v(51.35, 1.15) * mm});
            skLineSegment(sketch, "E354", {"start": v(51.35, 1.15) * mm, "end": v(51.47, 1.13) * mm});
            skLineSegment(sketch, "E355", {"start": v(51.47, 1.13) * mm, "end": v(51.48, 1.14) * mm});
            skLineSegment(sketch, "E356", {"start": v(51.48, 1.14) * mm, "end": v(51.5, 1.15) * mm});
            skLineSegment(sketch, "E357", {"start": v(51.5, 1.15) * mm, "end": v(51.7, 1.4) * mm});
            skLineSegment(sketch, "E358", {"start": v(51.7, 1.4) * mm, "end": v(52.27, 2.06) * mm});
            skLineSegment(sketch, "E359", {"start": v(52.27, 2.06) * mm, "end": v(53.06, 2.99) * mm});
            skLineSegment(sketch, "E360", {"start": v(53.06, 2.99) * mm, "end": v(53.96, 4.04) * mm});
            skLineSegment(sketch, "E361", {"start": v(53.96, 4.04) * mm, "end": v(54.85, 5.1) * mm});
            skLineSegment(sketch, "E362", {"start": v(54.85, 5.1) * mm, "end": v(55.64, 6.01) * mm});
            skLineSegment(sketch, "E363", {"start": v(55.64, 6.01) * mm, "end": v(56.2, 6.67) * mm});
            skLineSegment(sketch, "E364", {"start": v(56.2, 6.67) * mm, "end": v(56.4, 6.92) * mm});
            skLineSegment(sketch, "E365", {"start": v(56.4, 6.92) * mm, "end": v(56.42, 6.93) * mm});
            skLineSegment(sketch, "E366", {"start": v(56.42, 6.93) * mm, "end": v(56.47, 7) * mm});
            skLineSegment(sketch, "E367", {"start": v(56.47, 7) * mm, "end": v(56.48, 7.43) * mm});
            skLineSegment(sketch, "E368", {"start": v(56.48, 7.43) * mm, "end": v(56.12, 7.73) * mm});
            skLineSegment(sketch, "E369", {"start": v(56.12, 7.73) * mm, "end": v(56, 7.73) * mm});
            skLineSegment(sketch, "E370", {"start": v(56, 7.73) * mm, "end": v(54.24, 7.73) * mm});
            skLineSegment(sketch, "E371", {"start": v(54.24, 7.73) * mm, "end": v(54.24, 10.3) * mm});
            skLineSegment(sketch, "E372", {"start": v(54.24, 10.3) * mm, "end": v(65.88, 10.3) * mm});
            skLineSegment(sketch, "E373", {"start": v(65.88, 10.3) * mm, "end": v(65.88, 7.73) * mm});
            skLineSegment(sketch, "E374", {"start": v(65.88, 7.73) * mm, "end": v(63.28, 7.73) * mm});
            skLineSegment(sketch, "E375", {"start": v(63.28, 7.73) * mm, "end": v(63.13, 7.73) * mm});
            skLineSegment(sketch, "E376", {"start": v(63.13, 7.73) * mm, "end": v(62.66, 7.69) * mm});
            skLineSegment(sketch, "E377", {"start": v(62.66, 7.69) * mm, "end": v(62.17, 7.54) * mm});
            skLineSegment(sketch, "E378", {"start": v(62.17, 7.54) * mm, "end": v(61.73, 7.24) * mm});
            skLineSegment(sketch, "E379", {"start": v(61.73, 7.24) * mm, "end": v(61.36, 6.88) * mm});
            skLineSegment(sketch, "E380", {"start": v(61.36, 6.88) * mm, "end": v(61.24, 6.75) * mm});
            skLineSegment(sketch, "E381", {"start": v(61.24, 6.75) * mm, "end": v(61.16, 6.66) * mm});
            skLineSegment(sketch, "E382", {"start": v(61.16, 6.66) * mm, "end": v(60.82, 6.27) * mm});
            skLineSegment(sketch, "E383", {"start": v(60.82, 6.27) * mm, "end": v(59.9, 5.23) * mm});
            skLineSegment(sketch, "E384", {"start": v(59.9, 5.23) * mm, "end": v(58.67, 3.82) * mm});
            skLineSegment(sketch, "E385", {"start": v(58.67, 3.82) * mm, "end": v(57.28, 2.23) * mm});
            skLineSegment(sketch, "E386", {"start": v(57.28, 2.23) * mm, "end": v(55.89, 0.64) * mm});
            skLineSegment(sketch, "E387", {"start": v(55.89, 0.64) * mm, "end": v(54.67, -0.75) * mm});
            skLineSegment(sketch, "E388", {"start": v(54.67, -0.75) * mm, "end": v(53.78, -1.76) * mm});
            skLineSegment(sketch, "E389", {"start": v(53.78, -1.76) * mm, "end": v(53.45, -2.14) * mm});
            skLineSegment(sketch, "E390", {"start": v(53.45, -2.14) * mm, "end": v(53.4, -2.2) * mm});
            skLineSegment(sketch, "E391", {"start": v(53.4, -2.2) * mm, "end": v(53.38, -2.22) * mm});
            skLineSegment(sketch, "E392", {"start": v(53.38, -2.22) * mm, "end": v(53.3, -2.49) * mm});
            skLineSegment(sketch, "E393", {"start": v(53.3, -2.49) * mm, "end": v(53.3, -2.57) * mm});
            skLineSegment(sketch, "E394", {"start": v(53.3, -2.57) * mm, "end": v(53.3, -6.64) * mm});
            skLineSegment(sketch, "E395", {"start": v(53.3, -6.64) * mm, "end": v(53.3, -6.71) * mm});
            skLineSegment(sketch, "E396", {"start": v(53.3, -6.71) * mm, "end": v(53.32, -6.92) * mm});
            skLineSegment(sketch, "E397", {"start": v(53.32, -6.92) * mm, "end": v(53.35, -7.18) * mm});
            skLineSegment(sketch, "E398", {"start": v(53.35, -7.18) * mm, "end": v(53.36, -7.2) * mm});
            skLineSegment(sketch, "E399", {"start": v(53.36, -7.2) * mm, "end": v(53.39, -7.25) * mm});
            skLineSegment(sketch, "E400", {"start": v(53.39, -7.25) * mm, "end": v(53.85, -7.67) * mm});
            skLineSegment(sketch, "E401", {"start": v(53.85, -7.67) * mm, "end": v(53.92, -7.7) * mm});
            skLineSegment(sketch, "E402", {"start": v(53.92, -7.7) * mm, "end": v(53.95, -7.7) * mm});
            skLineSegment(sketch, "E403", {"start": v(53.95, -7.7) * mm, "end": v(54.27, -7.73) * mm});
            skLineSegment(sketch, "E404", {"start": v(54.27, -7.73) * mm, "end": v(54.54, -7.74) * mm});
            skLineSegment(sketch, "E405", {"start": v(54.54, -7.74) * mm, "end": v(54.63, -7.74) * mm});
            skLineSegment(sketch, "E406", {"start": v(54.63, -7.74) * mm, "end": v(57.3, -7.74) * mm});
            skLineSegment(sketch, "E407", {"start": v(57.3, -7.74) * mm, "end": v(57.3, -10.31) * mm});
            skLineSegment(sketch, "E408", {"start": v(57.3, -10.31) * mm, "end": v(43.16, -10.31) * mm});
            skLineSegment(sketch, "E409", {"start": v(43.16, -10.31) * mm, "end": v(43.16, -7.74) * mm});
            skLineSegment(sketch, "E410", {"start": v(43.16, -7.74) * mm, "end": v(45.68, -7.74) * mm});
            skSolve(sketch);
        }
        {
            var Q0;
            Q0 = qSketchRegion(id + "F4", true);
            extrude(context, id + "F5", {"entities" : qUnion([Q0]), "operationType" : NewBodyOperationType.REMOVE, "endBound" : BoundingType.SYMMETRIC, "depth" : 6.35 * mm, "offsetDistance" : 25.4 * mm});
        }
        {
            var Q0;
            Q0=qCreatedBy(id+"F1.planeOp",FACE);
            var sketch = newSketch(context, id + "F6", { "sketchPlane" : qUnion([Q0])});
            skLineSegment(sketch, "E411", {"start": v(2.54, -3.55) * mm, "end": v(2.54, -20.38) * mm});
            skLineSegment(sketch, "E412", {"start": v(9.17, -16.02) * mm, "end": v(2.54, -3.55) * mm});
            skPoint(sketch, "E413.visualSharp", {"position": v(11.13, -20.38) * mm});
            skArc(sketch, "E413.filletArc", {"start": v(7.54, -19.68) * mm, "mid": v(9.25, -18.25) * mm, "end": v(9.17, -16.02) * mm});
            skLineSegment(sketch, "E414", {"start": v(7.54, -19.68) * mm, "end": v(2.54, -20.38) * mm});
            skSolve(sketch);
        }
        {
            var Q0;
            Q0 = qSketchRegion(id + "F6", true);
            extrude(context, id + "F7", {"entities" : qUnion([Q0]), "operationType" : NewBodyOperationType.ADD, "depth" : 139.7 * mm, "offsetDistance" : 25.4 * mm});
        }
        {
            var Q0;
            Q0=qCreatedBy(makeId("Right.planeOp"),FACE);
            var sketch = newSketch(context, id + "F8", { "sketchPlane" : qUnion([Q0])});
            skLineSegment(sketch, "E415.bottom", {"start": v(16.07, -18.65) * mm, "end": v(-6.64, -21.46) * mm});
            skLineSegment(sketch, "E415.top", {"start": v(16.71, -23.82) * mm, "end": v(-6, -26.62) * mm});
            skLineSegment(sketch, "E415.left", {"start": v(16.07, -18.65) * mm, "end": v(16.71, -23.82) * mm});
            skLineSegment(sketch, "E415.right", {"start": v(-6.64, -21.46) * mm, "end": v(-6, -26.62) * mm});
            skSolve(sketch);
        }
        {
            var Q0;
            Q0=makeQuery(id+"F8.imprint","IMPRINT",FACE,{"disambiguationData":[TD([[makeQuery(id+"F8.imprint","IMPRINT",EDGE,{"derivedFrom":sQuery(id+"F8.wireOp",EDGE,"E415.bottom")}),1.0]])]});
            extrude(context, id + "F9", {"entities" : qUnion([Q0]), "operationType" : NewBodyOperationType.REMOVE, "endBound" : BoundingType.SYMMETRIC, "oppositeDirection" : true, "depth" : 254 * mm, "offsetDistance" : 25.4 * mm});
        }
        {
            var Q0;
            Q0=qCreatedBy(makeId("Top.planeOp"),FACE);
            var sketch = newSketch(context, id + "F10", { "sketchPlane" : qUnion([Q0])});
            skLineSegment(sketch, "E416.bottom", {"start": v(-67, 2.54) * mm, "end": v(67, 2.54) * mm});
            skLineSegment(sketch, "E416.top", {"start": v(-67, 29.8) * mm, "end": v(67, 29.8) * mm});
            skLineSegment(sketch, "E416.left", {"start": v(-67, 2.54) * mm, "end": v(-67, 29.8) * mm});
            skLineSegment(sketch, "E416.right", {"start": v(67, 2.54) * mm, "end": v(67, 29.8) * mm});
            skSolve(sketch);
        }
        {
            var Q0;
            Q0 = qSketchRegion(id + "F10", true);
            extrude(context, id + "F11", {"entities" : qUnion([Q0]), "operationType" : NewBodyOperationType.REMOVE, "oppositeDirection" : true, "depth" : 25.4 * mm, "offsetDistance" : 25.4 * mm});
        }
    });
